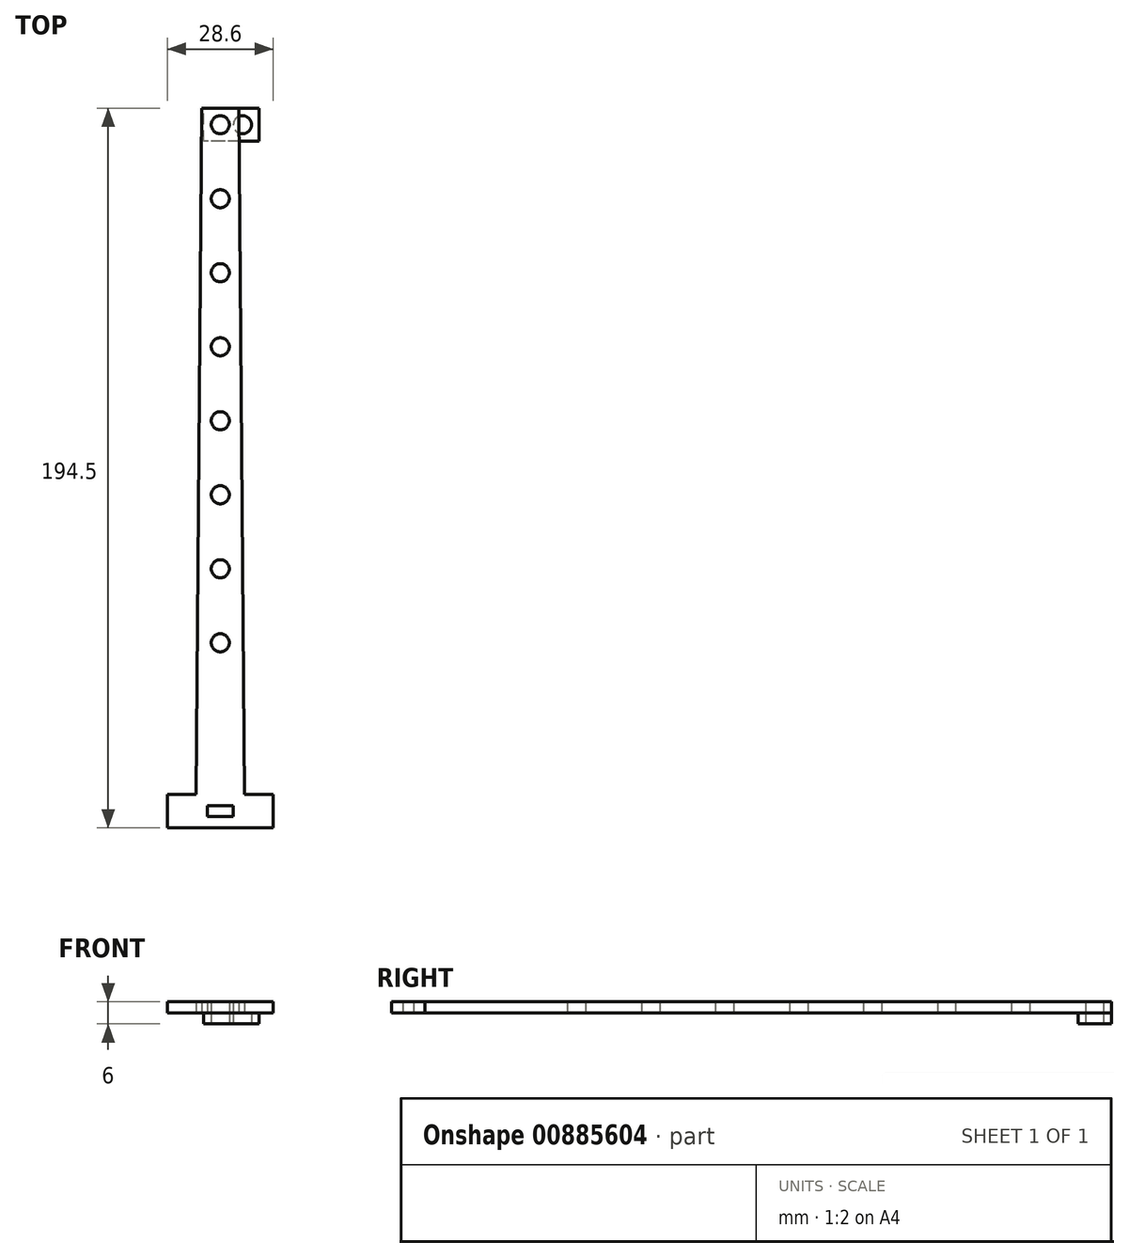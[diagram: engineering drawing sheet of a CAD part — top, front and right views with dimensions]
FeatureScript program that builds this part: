
annotation { "Feature Type Name" : "Feature", "Feature Type Description" : "" }
export const myFeature = defineFeature(function(context is Context, id is Id, definition is map)
    precondition{}
    {
        {
            var Q0;
            Q0=qCreatedBy(makeId("Top.planeOp"),FACE);
            var sketch = newSketch(context, id + "F0", { "sketchPlane" : qUnion([Q0])});
            skLineSegment(sketch, "E0.bottom", {"start": v(0, 0) * mm, "end": v(7.5, 0) * mm});
            skLineSegment(sketch, "E0.top", {"start": v(0, 9) * mm, "end": v(7.5, 9) * mm});
            skLineSegment(sketch, "E0.left", {"start": v(0, 0) * mm, "end": v(0, 9) * mm});
            skLineSegment(sketch, "E0.right", {"start": v(7.5, 0) * mm, "end": v(7.5, 9) * mm, "construction": true});
            skPoint(sketch, "E1.centerSnap0", {"position": v(0, 4.5) * mm});
            skPoint(sketch, "E2.centerSnap0", {"position": v(7.5, 4.5) * mm});
            skCircle(sketch, "E3", {"center": v(4.5, 4.5) * mm, "radius": 2.5 * mm, "construction": true});
            skPoint(sketch, "E3.centerSnap0", {"position": v(4.5, 9.63) * mm});
            skLineSegment(sketch, "E4.MirrorCS", {"start": v(15, 9) * mm, "end": v(7.5, 9) * mm});
            skLineSegment(sketch, "E5.MirrorCS", {"start": v(15, 0) * mm, "end": v(7.5, 0) * mm});
            skPoint(sketch, "E6.MirrorP", {"position": v(10.5, 9.63) * mm});
            skPoint(sketch, "E7.MirrorP", {"position": v(15, 4.5) * mm});
            skCircle(sketch, "E8.MirrorC", {"center": v(10.5, 4.5) * mm, "radius": 2.5 * mm, "construction": true});
            skLineSegment(sketch, "E9.MirrorCS", {"start": v(15, 0) * mm, "end": v(15, 9) * mm});
            skLineSegment(sketch, "E10.bottom", {"start": v(0, 0) * mm, "end": v(15, 0) * mm});
            skLineSegment(sketch, "E10.top", {"start": v(0, -5) * mm, "end": v(15, -5) * mm});
            skLineSegment(sketch, "E10.left", {"start": v(0, 0) * mm, "end": v(0, -5) * mm});
            skLineSegment(sketch, "E10.right", {"start": v(15, 0) * mm, "end": v(15, -5) * mm});
            skCircle(sketch, "E11.0", {"center": v(4.5, 4.5) * mm, "radius": 2.45 * mm});
            skCircle(sketch, "E12.MirrorC", {"center": v(10.5, 4.5) * mm, "radius": 2.45 * mm});
            skSolve(sketch);
        }
        {
            var Q0;
            Q0=makeQuery(id+"F0.imprint","IMPRINT",FACE,{"disambiguationData":[TD([[makeQuery(id+"F0.imprint","IMPRINT",EDGE,{"derivedFrom":sQuery(id+"F0.wireOp",EDGE,"E10.bottom")}),-1.0]])]});
            var Q1;
            Q1=makeQuery(id+"F0.imprint","IMPRINT",FACE,{"disambiguationData":[TD([[makeQuery(id+"F0.imprint","IMPRINT",EDGE,{"derivedFrom":sQuery(id+"F0.wireOp",EDGE,"E0.top")}),-1.0]])]});
            extrude(context, id + "F1", {"entities" : qUnion([Q0, Q1]), "depth" : 3 * mm, "offsetDistance" : 25 * mm});
        }
        {
            var Q0;
            Q0=makeQuery(id+"F1.opExtrude","CAP_FACE",FACE,{"disambiguationData":[OSD([sQuery(id+"F0.wireOp",EDGE,"E0.top"),sQuery(id+"F0.wireOp",EDGE,"E0.left"),sQuery(id+"F0.wireOp",EDGE,"E4.MirrorCS"),sQuery(id+"F0.wireOp",EDGE,"E9.MirrorCS"),sQuery(id+"F0.wireOp",EDGE,"E10.top"),sQuery(id+"F0.wireOp",EDGE,"E10.left"),sQuery(id+"F0.wireOp",EDGE,"E10.right"),sQuery(id+"F0.wireOp",EDGE,"E11.0"),sQuery(id+"F0.wireOp",EDGE,"E12.MirrorC")])],"isStart":false});
            var sketch = newSketch(context, id + "F2", { "sketchPlane" : qUnion([Q0])});
            skCircle(sketch, "E13.0", {"center": v(4.5, 4.5) * mm, "radius": 2.45 * mm});
            skLineSegment(sketch, "E14.bottom", {"start": v(0, 9) * mm, "end": v(4.5, 9) * mm});
            skLineSegment(sketch, "E14.top", {"start": v(0, 4.5) * mm, "end": v(4.5, 4.5) * mm, "construction": true});
            skLineSegment(sketch, "E14.left", {"start": v(0, 9) * mm, "end": v(0, 4.5) * mm, "construction": true});
            skLineSegment(sketch, "E14.right", {"start": v(4.5, 9) * mm, "end": v(4.5, 4.5) * mm, "construction": true});
            skLineSegment(sketch, "E15.MirrorCS", {"start": v(9, 9) * mm, "end": v(4.5, 9) * mm});
            skLineSegment(sketch, "E16.MirrorCS", {"start": v(9, 9) * mm, "end": v(9, 4.5) * mm, "construction": true});
            skLineSegment(sketch, "E17.MirrorCS", {"start": v(0, 0) * mm, "end": v(4.5, 0) * mm});
            skLineSegment(sketch, "E18.MirrorCS", {"start": v(9, 0) * mm, "end": v(4.5, 0) * mm});
            skLineSegment(sketch, "E19.MirrorCS", {"start": v(0, 0) * mm, "end": v(0, 4.5) * mm, "construction": true});
            skLineSegment(sketch, "E20.MirrorCS", {"start": v(9, 0) * mm, "end": v(9, 4.5) * mm, "construction": true});
            skLineSegment(sketch, "E21.bottom", {"start": v(-0.5, 0) * mm, "end": v(9.5, 0) * mm});
            skLineSegment(sketch, "E21.top", {"start": v(-0.5, 9) * mm, "end": v(9.5, 9) * mm});
            skLineSegment(sketch, "E21.left", {"start": v(-0.5, 0) * mm, "end": v(-0.5, 9) * mm});
            skLineSegment(sketch, "E21.right", {"start": v(9.5, 0) * mm, "end": v(9.5, 9) * mm});
            skPoint(sketch, "E22", {"position": v(4.5, 0) * mm});
            skLineSegment(sketch, "E23.left", {"start": v(-0.5, 0) * mm, "end": v(-0.5, 0) * mm});
            skLineSegment(sketch, "E23.right", {"start": v(9.5, 0) * mm, "end": v(9.5, 0) * mm});
            skLineSegment(sketch, "E24.bottom", {"start": v(9.5, 0) * mm, "end": v(-0.5, 0) * mm});
            skLineSegment(sketch, "E24.top", {"start": v(9.5, -185.5) * mm, "end": v(-0.5, -185.5) * mm});
            skLineSegment(sketch, "E24.left", {"start": v(9.5, 0) * mm, "end": v(9.5, -185.5) * mm, "construction": true});
            skLineSegment(sketch, "E24.right", {"start": v(-0.5, 0) * mm, "end": v(-0.5, -185.5) * mm, "construction": true});
            skCircle(sketch, "E25.0.1.0", {"center": v(4.5, -15.5) * mm, "radius": 2.45 * mm});
            skCircle(sketch, "E25.0.2.0", {"center": v(4.5, -35.5) * mm, "radius": 2.45 * mm});
            skCircle(sketch, "E25.0.3.0", {"center": v(4.5, -55.5) * mm, "radius": 2.45 * mm});
            skCircle(sketch, "E25.0.4.0", {"center": v(4.5, -75.5) * mm, "radius": 2.45 * mm});
            skCircle(sketch, "E25.0.5.0", {"center": v(4.5, -95.5) * mm, "radius": 2.45 * mm});
            skCircle(sketch, "E25.0.6.0", {"center": v(4.5, -115.5) * mm, "radius": 2.45 * mm});
            skCircle(sketch, "E25.0.7.0", {"center": v(4.5, -135.5) * mm, "radius": 2.45 * mm});
            skLineSegment(sketch, "E25.direction1", {"start": v(4.5, 4.5) * mm, "end": v(21.4, 4.5) * mm, "construction": true});
            skLineSegment(sketch, "E25.direction2", {"start": v(4.5, 4.5) * mm, "end": v(4.5, -15.5) * mm, "construction": true});
            skLineSegment(sketch, "E26.bottom", {"start": v(4.5, -185.5) * mm, "end": v(-2, -185.5) * mm});
            skLineSegment(sketch, "E26.top", {"start": v(4.5, -176.5) * mm, "end": v(-2, -176.5) * mm});
            skLineSegment(sketch, "E26.left", {"start": v(4.5, -185.5) * mm, "end": v(4.5, -176.5) * mm, "construction": true});
            skLineSegment(sketch, "E26.right", {"start": v(-2, -185.5) * mm, "end": v(-2, -176.5) * mm});
            skLineSegment(sketch, "E27.bottom", {"start": v(1, -179.5) * mm, "end": v(8, -179.5) * mm});
            skLineSegment(sketch, "E27.top", {"start": v(1, -182.5) * mm, "end": v(8, -182.5) * mm});
            skLineSegment(sketch, "E27.left", {"start": v(1, -179.5) * mm, "end": v(1, -182.5) * mm});
            skLineSegment(sketch, "E27.right", {"start": v(8, -179.5) * mm, "end": v(8, -182.5) * mm});
            skPoint(sketch, "E28", {"position": v(4.5, -182.5) * mm});
            skLineSegment(sketch, "E29.MirrorCS", {"start": v(4.5, -176.5) * mm, "end": v(11, -176.5) * mm});
            skLineSegment(sketch, "E30.MirrorCS", {"start": v(11, -185.5) * mm, "end": v(11, -176.5) * mm});
            skLineSegment(sketch, "E31.MirrorCS", {"start": v(4.5, -185.5) * mm, "end": v(11, -185.5) * mm});
            skLineSegment(sketch, "E32", {"start": v(9.5, 9) * mm, "end": v(11, -176.5) * mm});
            skLineSegment(sketch, "E33", {"start": v(-2, -176.5) * mm, "end": v(-0.5, 9) * mm});
            skLineSegment(sketch, "E34.bottom", {"start": v(4.5, -176.5) * mm, "end": v(-9.8, -176.5) * mm});
            skLineSegment(sketch, "E34.top", {"start": v(4.5, -185.5) * mm, "end": v(-9.8, -185.5) * mm});
            skLineSegment(sketch, "E34.left", {"start": v(4.5, -176.5) * mm, "end": v(4.5, -185.5) * mm});
            skLineSegment(sketch, "E34.right", {"start": v(-9.8, -176.5) * mm, "end": v(-9.8, -185.5) * mm});
            skLineSegment(sketch, "E35.MirrorCS", {"start": v(4.5, -176.5) * mm, "end": v(18.8, -176.5) * mm});
            skLineSegment(sketch, "E36.MirrorCS", {"start": v(18.8, -176.5) * mm, "end": v(18.8, -185.5) * mm});
            skLineSegment(sketch, "E37.MirrorCS", {"start": v(4.5, -185.5) * mm, "end": v(18.8, -185.5) * mm});
            skSolve(sketch);
        }
        {
            var Q0;
            Q0 = qSketchRegion(id + "F2", true);
            extrude(context, id + "F3", {"entities" : qUnion([Q0]), "depth" : 3 * mm, "offsetDistance" : 25 * mm});
        }
    });
